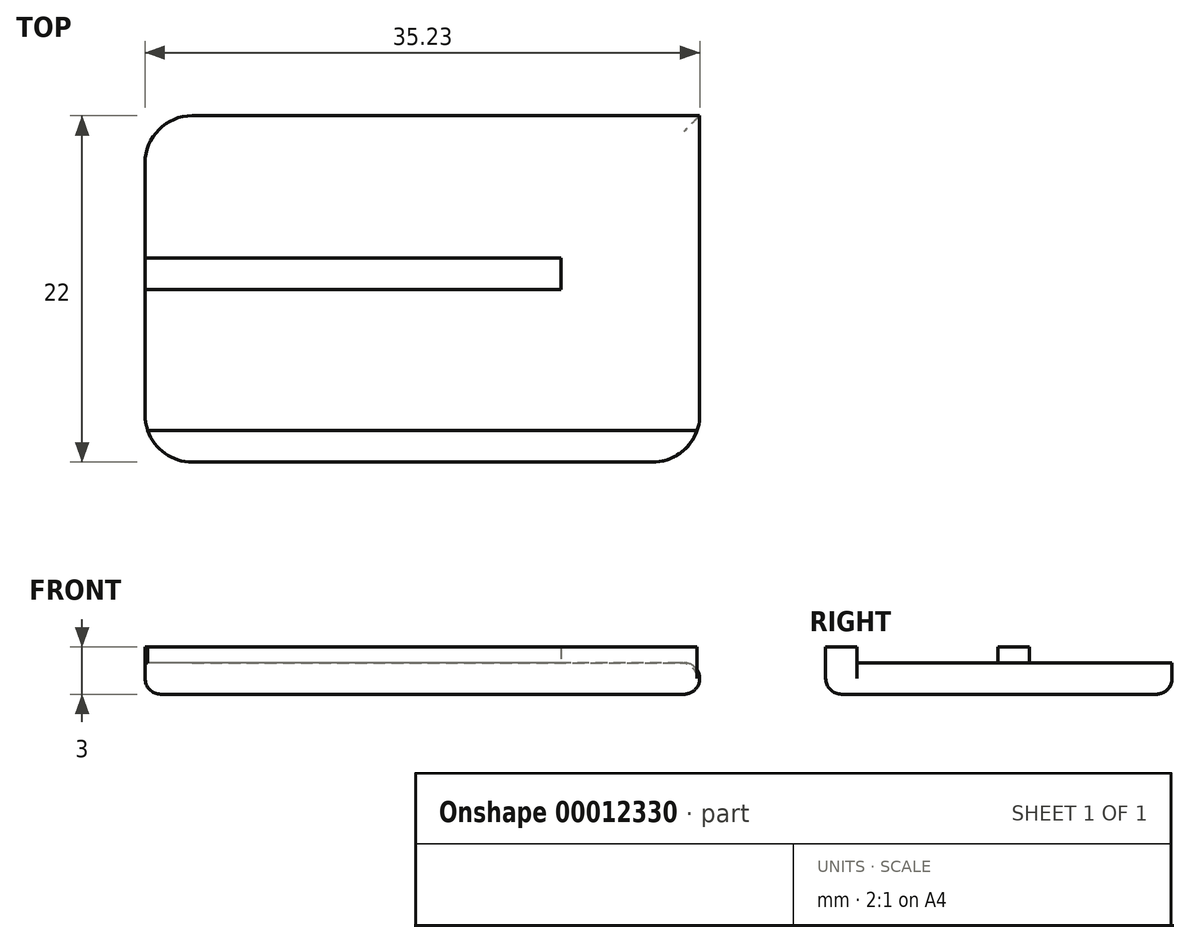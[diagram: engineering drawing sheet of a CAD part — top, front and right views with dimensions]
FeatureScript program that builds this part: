
annotation { "Feature Type Name" : "Feature", "Feature Type Description" : "" }
export const myFeature = defineFeature(function(context is Context, id is Id, definition is map)
    precondition{}
    {
        {
            var Q0;
            Q0=qCreatedBy(makeId("Top.planeOp"),FACE);
            var sketch = newSketch(context, id + "F0", { "sketchPlane" : qUnion([Q0])});
            skLineSegment(sketch, "E0.bottom", {"start": v(-5.87, 15.39) * mm, "end": v(31.13, 15.39) * mm});
            skLineSegment(sketch, "E0.top", {"start": v(-5.87, -6.61) * mm, "end": v(31.13, -6.61) * mm});
            skLineSegment(sketch, "E0.left", {"start": v(-5.87, 15.39) * mm, "end": v(-5.87, -6.61) * mm});
            skLineSegment(sketch, "E0.right", {"start": v(31.13, 15.39) * mm, "end": v(31.13, -6.61) * mm});
            skLineSegment(sketch, "E1", {"start": v(29.36, 15.39) * mm, "end": v(29.36, -6.61) * mm});
            skLineSegment(sketch, "E2", {"start": v(29.36, 5.33) * mm, "end": v(-5.87, 5.33) * mm, "construction": true});
            skLineSegment(sketch, "E3.0", {"start": v(29.36, 6.33) * mm, "end": v(-5.87, 6.33) * mm});
            skLineSegment(sketch, "E4.0", {"start": v(29.36, 4.33) * mm, "end": v(-5.87, 4.33) * mm});
            skLineSegment(sketch, "E5.bottom", {"start": v(29.36, -6.61) * mm, "end": v(-5.87, -6.61) * mm});
            skLineSegment(sketch, "E5.top", {"start": v(29.36, -4.61) * mm, "end": v(-5.87, -4.61) * mm});
            skLineSegment(sketch, "E5.left", {"start": v(29.36, -6.61) * mm, "end": v(29.36, -4.61) * mm});
            skLineSegment(sketch, "E5.right", {"start": v(-5.87, -6.61) * mm, "end": v(-5.87, -4.61) * mm});
            skLineSegment(sketch, "E6", {"start": v(20.54, 6.33) * mm, "end": v(20.54, 4.33) * mm});
            skSolve(sketch);
        }
        {
            var Q0;
            {var subQ0=sQuery(id+"F0.wireOp",EDGE,"E3.0");Q0=makeQuery(id+"F0.imprint","IMPRINT",FACE,{"disambiguationData":[TD([[makeQuery(id+"F0.imprint","IMPRINT",EDGE,{"derivedFrom":subQ0}),-1.0]])]});}
            var Q1;
            {var subQ0=sQuery(id+"F0.wireOp",EDGE,"E4.0");Q1=makeQuery(id+"F0.imprint","IMPRINT",FACE,{"disambiguationData":[TD([[makeQuery(id+"F0.imprint","IMPRINT",EDGE,{"derivedFrom":subQ0}),1.0]])]});}
            var Q2;
            {var subQ0=sQuery(id+"F0.wireOp",EDGE,"E6");Q2=makeQuery(id+"F0.imprint","IMPRINT",FACE,{"disambiguationData":[TD([[makeQuery(id+"F0.imprint","IMPRINT",EDGE,{"derivedFrom":subQ0}),1.0]])]});}
            extrude(context, id + "F1", {"entities" : qUnion([Q0, Q1, Q2]), "depth" : 2 * mm});
        }
        {
            var Q0;
            {var subQ1=sQuery(id+"F0.wireOp",EDGE,"E6");Q0=makeQuery(id+"F0.imprint","IMPRINT",FACE,{"disambiguationData":[TD([[makeQuery(id+"F0.imprint","IMPRINT",EDGE,{"derivedFrom":subQ1}),-1.0]])]});}
            var Q1;
            Q1=makeQuery(id+"F0.imprint","IMPRINT",FACE,{"disambiguationData":[TD([[makeQuery(id+"F0.imprint","IMPRINT",EDGE,{"derivedFrom":sQuery(id+"F0.wireOp",EDGE,"E0.top")}),1.0]])]});
            var Q2;
            Q2=makeQuery(id+"F0.imprint","IMPRINT",FACE,{"disambiguationData":[TD([[makeQuery(id+"F0.imprint","IMPRINT",EDGE,{"derivedFrom":sQuery(id+"F0.wireOp",EDGE,"E5.bottom")}),-1.0]])]});
            extrude(context, id + "F2", {"entities" : qUnion([Q0, Q1, Q2]), "operationType" : NewBodyOperationType.ADD, "depth" : 3 * mm});
        }
        {
            var Q0;
            Q0=makeQuery(id+"F2.opExtrude","SWEPT_EDGE",EDGE,{"disambiguationData":[OSD([sQuery(id+"F0.wireOp",EDGE,"E0.bottom"),sQuery(id+"F0.wireOp",EDGE,"E0.right")])]});
            var Q1;
            Q1=makeQuery(id+"F2.opExtrude","SWEPT_EDGE",EDGE,{"disambiguationData":[OSD([sQuery(id+"F0.wireOp",EDGE,"E0.top"),sQuery(id+"F0.wireOp",EDGE,"E0.right")])]});
            var Q2;
            Q2=makeQuery(id+"F1.opExtrude","SWEPT_EDGE",EDGE,{"disambiguationData":[OSD([sQuery(id+"F0.wireOp",EDGE,"E0.bottom"),sQuery(id+"F0.wireOp",EDGE,"E0.left")])]});
            var Q3;
            Q3=makeQuery(id+"F2.opExtrude","SWEPT_EDGE",EDGE,{"disambiguationData":[OSD([sQuery(id+"F0.wireOp",EDGE,"E5.bottom"),sQuery(id+"F0.wireOp",EDGE,"E5.right")])]});
            fillet(context, id + "F3", {"entities" : qUnion([Q0, Q1, Q2, Q3]), "radius" : 3 * mm, "tangentPropagation" : true, "allowEdgeOverflow" : false});
        }
        {
            var Q0;
            Q0=makeQuery(id+"F1.opExtrude","CAP_EDGE",EDGE,{"disambiguationData":[OSD([sQuery(id+"F0.wireOp",EDGE,"E4.0")])],"isStart":false});
            var Q1;
            Q1=makeQuery(id+"F1.opExtrude","CAP_EDGE",EDGE,{"disambiguationData":[OSD([sQuery(id+"F0.wireOp",EDGE,"E6")])],"isStart":false});
            var Q2;
            Q2=makeQuery(id+"F1.opExtrude","CAP_EDGE",EDGE,{"disambiguationData":[OSD([sQuery(id+"F0.wireOp",EDGE,"E1")])],"isStart":false});
            var Q3;
            Q3=makeQuery(id+"F1.opExtrude","CAP_EDGE",EDGE,{"disambiguationData":[OSD([sQuery(id+"F0.wireOp",EDGE,"E5.top")])],"isStart":false});
            var Q4;
            Q4=makeQuery(id+"F1.opExtrude","CAP_EDGE",EDGE,{"disambiguationData":[OSD([sQuery(id+"F0.wireOp",EDGE,"E3.0")])],"isStart":false});
            var Q5;
            {var subQ0=sQuery(id+"F0.wireOp",EDGE,"E0.bottom");var subQ1=sQuery(id+"F0.wireOp",EDGE,"E0.left");var subQ2=sQuery(id+"F0.wireOp",EDGE,"E1");var subQ3=sQuery(id+"F0.wireOp",EDGE,"E3.0");var subQ4=sQuery(id+"F0.wireOp",EDGE,"E4.0");var subQ5=sQuery(id+"F0.wireOp",EDGE,"E5.top");var subQ6=sQuery(id+"F0.wireOp",EDGE,"E6");Q5=makeQuery(id+"F2.boolean.opBoolean","MERGE",FACE,{"derivedFrom":[makeQuery(id+"F1.opExtrude","CAP_FACE",FACE,{"disambiguationData":[OSD([subQ0,subQ1,subQ2,subQ3,subQ4,subQ5,subQ6])],"isStart":true}),makeQuery(id+"F2.opExtrude","CAP_FACE",FACE,{"disambiguationData":[OSD([subQ0,sQuery(id+"F0.wireOp",EDGE,"E0.top"),sQuery(id+"F0.wireOp",EDGE,"E0.right"),subQ2,sQuery(id+"F0.wireOp",EDGE,"E5.bottom"),subQ5,sQuery(id+"F0.wireOp",EDGE,"E5.right")])],"isStart":true}),makeQuery(id+"F2.opExtrude","CAP_FACE",FACE,{"disambiguationData":[OSD([subQ1,subQ3,subQ4,subQ6])],"isStart":true})]});}
            fillet(context, id + "F4", {"entities" : qUnion([Q0, Q1, Q2, Q3, Q4, Q5]), "radius" : 1 * mm, "tangentPropagation" : true, "allowEdgeOverflow" : false});
        }
    });
